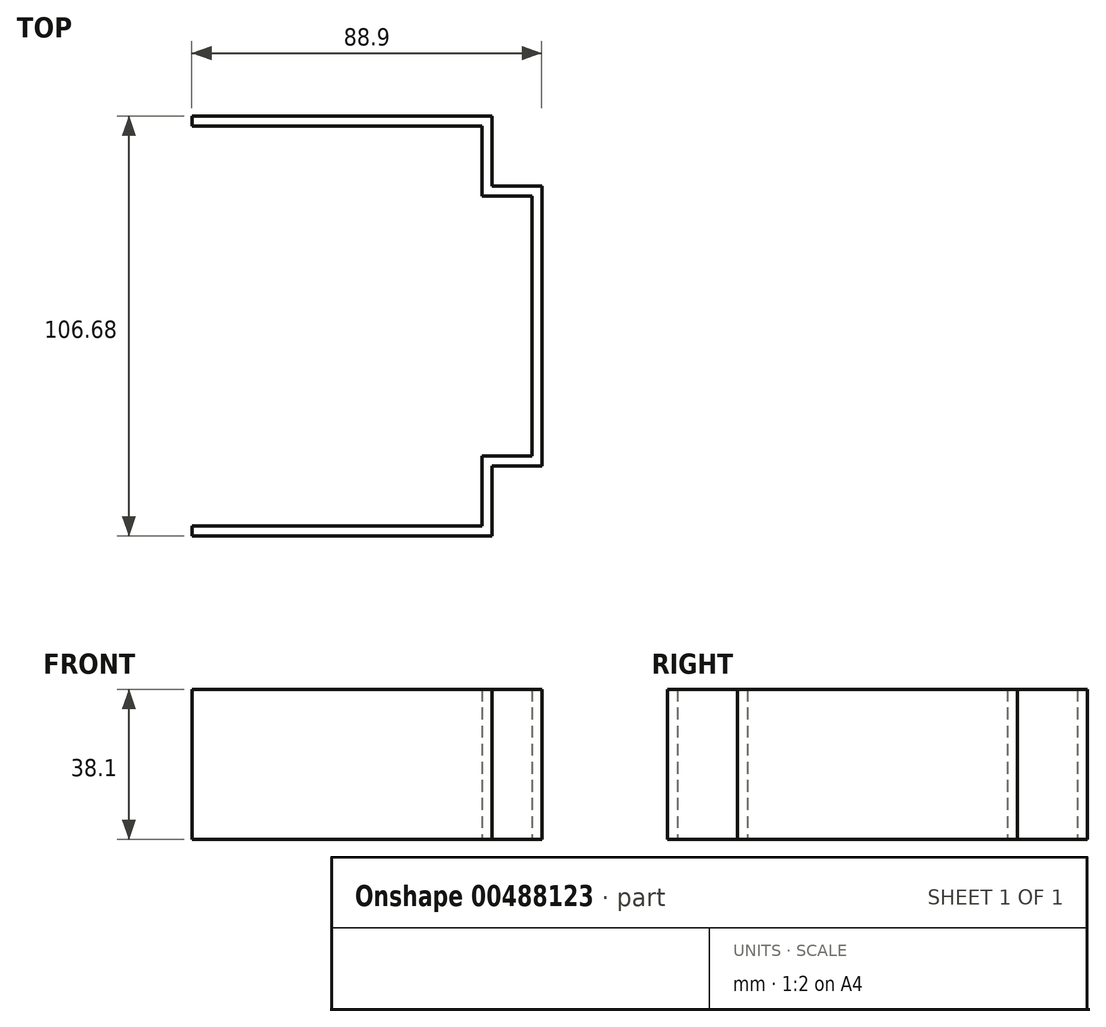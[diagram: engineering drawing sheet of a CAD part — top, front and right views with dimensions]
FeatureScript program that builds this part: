
annotation { "Feature Type Name" : "Feature", "Feature Type Description" : "" }
export const myFeature = defineFeature(function(context is Context, id is Id, definition is map)
    precondition{}
    {
        {
            var Q0;
            Q0=qCreatedBy(makeId("Top.planeOp"),FACE);
            var sketch = newSketch(context, id + "F0", { "sketchPlane" : qUnion([Q0])});
            skLineSegment(sketch, "E0", {"start": v(-84.7, 40.06) * mm, "end": v(-8.5, 40.06) * mm});
            skLineSegment(sketch, "E1", {"start": v(-8.5, 40.06) * mm, "end": v(-8.5, 22.28) * mm});
            skLineSegment(sketch, "E2", {"start": v(-8.5, 22.28) * mm, "end": v(4.2, 22.28) * mm});
            skLineSegment(sketch, "E3", {"start": v(4.2, 22.28) * mm, "end": v(4.2, -48.84) * mm});
            skLineSegment(sketch, "E4", {"start": v(4.2, -48.84) * mm, "end": v(-8.5, -48.84) * mm});
            skLineSegment(sketch, "E5", {"start": v(-8.5, -48.84) * mm, "end": v(-8.5, -66.62) * mm});
            skLineSegment(sketch, "E6", {"start": v(-8.5, -66.62) * mm, "end": v(-84.7, -66.62) * mm});
            skLineSegment(sketch, "E7", {"start": v(-84.7, -66.62) * mm, "end": v(-84.7, -64.08) * mm});
            skLineSegment(sketch, "E8", {"start": v(-84.7, -64.08) * mm, "end": v(-11.05, -64.08) * mm});
            skLineSegment(sketch, "E9", {"start": v(-11.05, -64.08) * mm, "end": v(-11.05, -46.3) * mm});
            skLineSegment(sketch, "E10", {"start": v(-11.05, -46.3) * mm, "end": v(1.65, -46.3) * mm});
            skLineSegment(sketch, "E11", {"start": v(1.65, -46.3) * mm, "end": v(1.65, 19.74) * mm});
            skLineSegment(sketch, "E12", {"start": v(1.65, 19.74) * mm, "end": v(-11.05, 19.74) * mm});
            skLineSegment(sketch, "E13", {"start": v(-11.05, 19.74) * mm, "end": v(-11.05, 37.52) * mm});
            skLineSegment(sketch, "E14", {"start": v(-11.05, 37.52) * mm, "end": v(-84.7, 37.52) * mm});
            skLineSegment(sketch, "E15", {"start": v(-84.7, 37.52) * mm, "end": v(-84.7, 40.06) * mm});
            skSolve(sketch);
        }
        {
            var Q0;
            Q0=makeQuery(id+"F0.imprint","IMPRINT",FACE,{"disambiguationData":[TD([[makeQuery(id+"F0.imprint","IMPRINT",EDGE,{"derivedFrom":sQuery(id+"F0.wireOp",EDGE,"E0")}),-1.0]])]});
            extrude(context, id + "F1", {"entities" : qUnion([Q0]), "depth" : 38.1 * mm, "offsetDistance" : 25.4 * mm});
        }
    });
